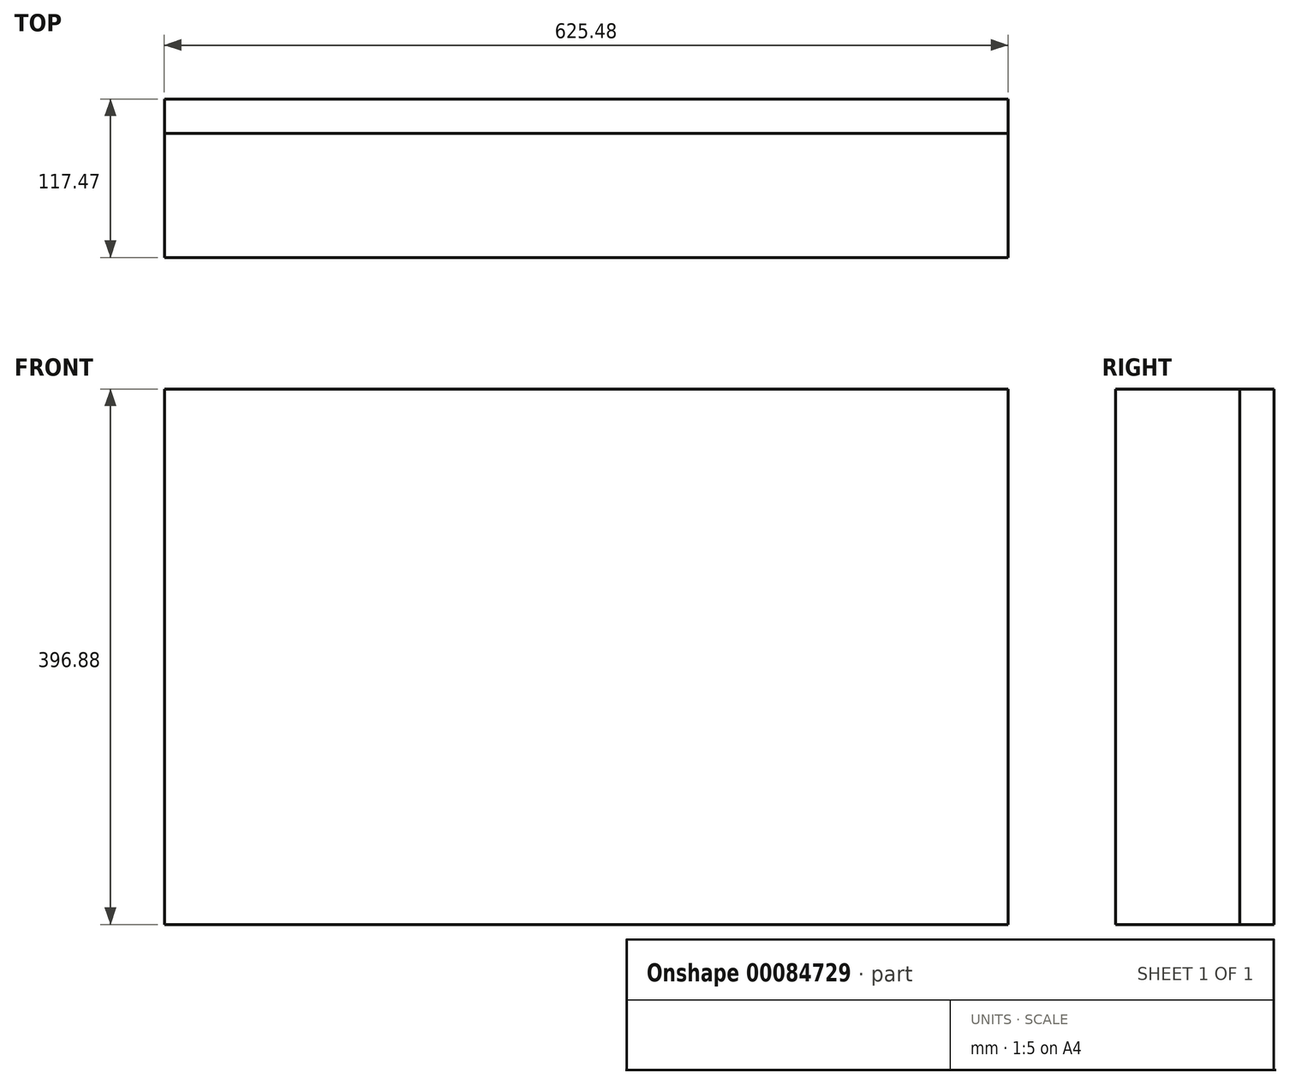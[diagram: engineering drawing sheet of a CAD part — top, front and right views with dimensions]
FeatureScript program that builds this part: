
annotation { "Feature Type Name" : "Feature", "Feature Type Description" : "" }
export const myFeature = defineFeature(function(context is Context, id is Id, definition is map)
    precondition{}
    {
        {
            var Q0;
            Q0=qCreatedBy(makeId("Front.planeOp"),FACE);
            var sketch = newSketch(context, id + "F0", { "sketchPlane" : qUnion([Q0])});
            skLineSegment(sketch, "E0.bottom", {"start": v(-312.74, 198.44) * mm, "end": v(312.74, 198.44) * mm});
            skLineSegment(sketch, "E0.top", {"start": v(-312.74, -198.44) * mm, "end": v(312.74, -198.44) * mm});
            skLineSegment(sketch, "E0.left", {"start": v(-312.74, 198.44) * mm, "end": v(-312.74, -198.44) * mm});
            skLineSegment(sketch, "E0.right", {"start": v(312.74, 198.44) * mm, "end": v(312.74, -198.44) * mm});
            skSolve(sketch);
        }
        {
            var Q0;
            Q0=makeQuery(id+"F0.imprint","IMPRINT",FACE,{"disambiguationData":[TD([[makeQuery(id+"F0.imprint","IMPRINT",EDGE,{"derivedFrom":sQuery(id+"F0.wireOp",EDGE,"E0.bottom")}),-1.0]])]});
            extrude(context, id + "F1", {"entities" : qUnion([Q0]), "depth" : 25.4 * mm});
        }
        {
            var Q0;
            Q0=makeQuery(id+"F1.opExtrude","CAP_FACE",FACE,{"disambiguationData":[OSD([sQuery(id+"F0.wireOp",EDGE,"E0.bottom"),sQuery(id+"F0.wireOp",EDGE,"E0.top"),sQuery(id+"F0.wireOp",EDGE,"E0.left"),sQuery(id+"F0.wireOp",EDGE,"E0.right")])],"isStart":false});
            var sketch = newSketch(context, id + "F2", { "sketchPlane" : qUnion([Q0])});
            skLineSegment(sketch, "E1.bottom", {"start": v(-312.74, 198.44) * mm, "end": v(312.74, 198.44) * mm});
            skLineSegment(sketch, "E1.top", {"start": v(-312.74, -198.44) * mm, "end": v(312.74, -198.44) * mm});
            skLineSegment(sketch, "E1.left", {"start": v(-312.74, 198.44) * mm, "end": v(-312.74, -198.44) * mm});
            skLineSegment(sketch, "E1.right", {"start": v(312.74, 198.44) * mm, "end": v(312.74, -198.44) * mm});
            skSolve(sketch);
        }
        {
            var Q0;
            Q0=makeQuery(id+"F2.imprint","IMPRINT",FACE,{"disambiguationData":[TD([[makeQuery(id+"F2.imprint","IMPRINT",EDGE,{"derivedFrom":sQuery(id+"F2.wireOp",EDGE,"E1.bottom")}),-1.0]])]});
            extrude(context, id + "F3", {"entities" : qUnion([Q0]), "depth" : 92.07 * mm});
        }
    });
